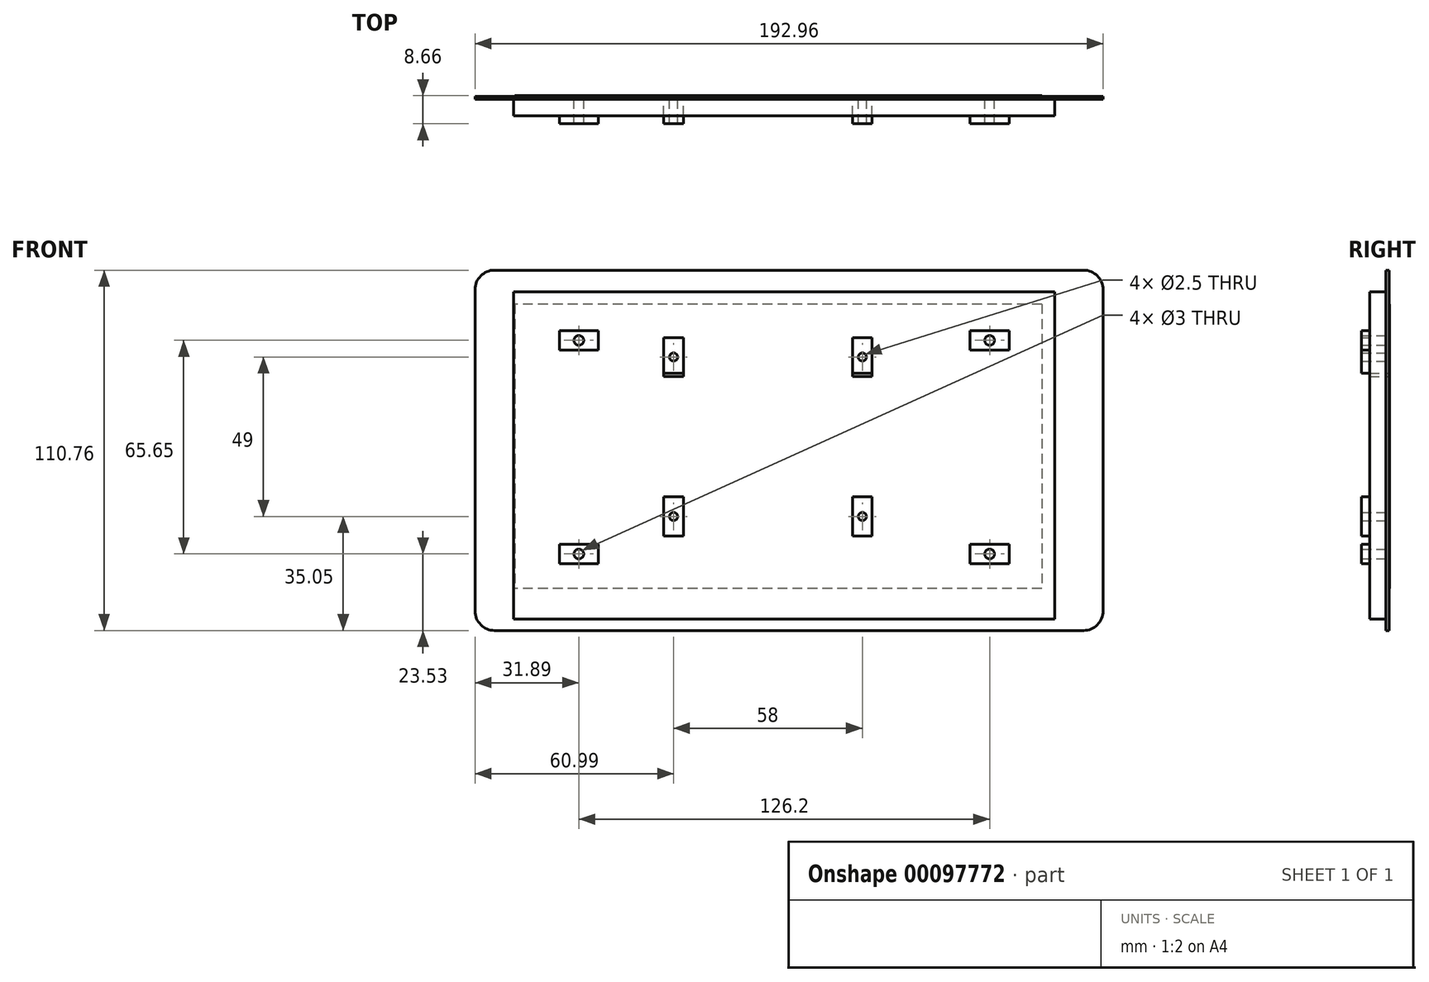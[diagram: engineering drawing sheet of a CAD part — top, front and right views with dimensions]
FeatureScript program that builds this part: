
annotation { "Feature Type Name" : "Feature", "Feature Type Description" : "" }
export const myFeature = defineFeature(function(context is Context, id is Id, definition is map)
    precondition{}
    {
        {
            var Q0;
            Q0=qCreatedBy(makeId("Front.planeOp"),FACE);
            var sketch = newSketch(context, id + "F0", { "sketchPlane" : qUnion([Q0])});
            skLineSegment(sketch, "E0.bottom", {"start": v(90.48, 55.38) * mm, "end": v(-90.48, 55.38) * mm});
            skLineSegment(sketch, "E0.top", {"start": v(90.48, -55.38) * mm, "end": v(-90.48, -55.38) * mm});
            skLineSegment(sketch, "E0.left", {"start": v(96.48, 49.38) * mm, "end": v(96.48, -49.38) * mm});
            skLineSegment(sketch, "E0.right", {"start": v(-96.48, 49.38) * mm, "end": v(-96.48, -49.38) * mm});
            skPoint(sketch, "E0.middle", {"position": v(0, 0) * mm});
            skPoint(sketch, "E1.visualSharp", {"position": v(-96.48, 55.38) * mm});
            skArc(sketch, "E1.filletArc", {"start": v(-90.48, 55.38) * mm, "mid": v(-94.72, 53.62) * mm, "end": v(-96.48, 49.38) * mm});
            skPoint(sketch, "E2.visualSharp", {"position": v(96.48, 55.38) * mm});
            skArc(sketch, "E2.filletArc", {"start": v(96.48, 49.38) * mm, "mid": v(94.72, 53.62) * mm, "end": v(90.48, 55.38) * mm});
            skPoint(sketch, "E3.visualSharp", {"position": v(96.48, -55.38) * mm});
            skArc(sketch, "E3.filletArc", {"start": v(90.48, -55.38) * mm, "mid": v(94.72, -53.62) * mm, "end": v(96.48, -49.38) * mm});
            skPoint(sketch, "E4.visualSharp", {"position": v(-96.48, -55.38) * mm});
            skArc(sketch, "E4.filletArc", {"start": v(-96.48, -49.38) * mm, "mid": v(-94.72, -53.62) * mm, "end": v(-90.48, -55.38) * mm});
            skLineSegment(sketch, "E5", {"start": v(-96.48, 39.83) * mm, "end": v(-84.6, 39.83) * mm});
            skLineSegment(sketch, "E6", {"start": v(-83.46, 55.38) * mm, "end": v(-83.46, 48.75) * mm});
            skLineSegment(sketch, "E7.bottom", {"start": v(-84.6, 48.75) * mm, "end": v(81.6, 48.75) * mm});
            skLineSegment(sketch, "E7.top", {"start": v(-84.6, -51.85) * mm, "end": v(81.6, -51.85) * mm});
            skLineSegment(sketch, "E7.left", {"start": v(-84.6, 48.75) * mm, "end": v(-84.6, -51.85) * mm});
            skLineSegment(sketch, "E7.right", {"start": v(81.6, 48.75) * mm, "end": v(81.6, -51.85) * mm});
            skLineSegment(sketch, "E8", {"start": v(-84.6, 23.64) * mm, "end": v(-64.6, 23.64) * mm});
            skLineSegment(sketch, "E9", {"start": v(-64.6, 23.64) * mm, "end": v(61.6, 23.64) * mm});
            skLineSegment(sketch, "E10", {"start": v(61.6, 23.64) * mm, "end": v(9.4, 23.64) * mm});
            skLineSegment(sketch, "E11", {"start": v(76.4, 55.38) * mm, "end": v(76.4, 33.8) * mm});
            skLineSegment(sketch, "E12", {"start": v(76.4, 33.8) * mm, "end": v(76.4, -31.85) * mm});
            skLineSegment(sketch, "E13", {"start": v(-84.6, 7.67) * mm, "end": v(-83.94, 7.67) * mm});
            skCircle(sketch, "E14", {"center": v(61.6, 33.8) * mm, "radius": 1.5 * mm});
            skCircle(sketch, "E15", {"center": v(-64.6, 33.8) * mm, "radius": 1.5 * mm});
            skCircle(sketch, "E16", {"center": v(61.6, -31.85) * mm, "radius": 1.5 * mm});
            skCircle(sketch, "E17", {"center": v(-64.6, -31.85) * mm, "radius": 1.5 * mm});
            skLineSegment(sketch, "E18", {"start": v(55.09, 48.75) * mm, "end": v(55.09, 28.67) * mm});
            skLineSegment(sketch, "E19", {"start": v(55.09, 28.67) * mm, "end": v(55.09, -20.33) * mm});
            skLineSegment(sketch, "E20", {"start": v(-83.94, 7.67) * mm, "end": v(-35.5, 7.67) * mm});
            skLineSegment(sketch, "E21", {"start": v(-35.5, 7.67) * mm, "end": v(22.5, 7.67) * mm});
            skCircle(sketch, "E22", {"center": v(22.5, 28.67) * mm, "radius": 1.25 * mm});
            skCircle(sketch, "E23", {"center": v(-35.5, 28.67) * mm, "radius": 1.25 * mm});
            skCircle(sketch, "E24", {"center": v(-35.5, -20.33) * mm, "radius": 1.25 * mm});
            skCircle(sketch, "E25", {"center": v(22.5, -20.33) * mm, "radius": 1.25 * mm});
            skLineSegment(sketch, "E26.bottom", {"start": v(-58.6, 36.8) * mm, "end": v(-70.6, 36.8) * mm});
            skLineSegment(sketch, "E26.top", {"start": v(-58.6, 30.8) * mm, "end": v(-70.6, 30.8) * mm});
            skLineSegment(sketch, "E26.left", {"start": v(-58.6, 36.8) * mm, "end": v(-58.6, 30.8) * mm});
            skLineSegment(sketch, "E26.right", {"start": v(-70.6, 36.8) * mm, "end": v(-70.6, 30.8) * mm});
            skLineSegment(sketch, "E27.bottom", {"start": v(67.61, 30.8) * mm, "end": v(55.61, 30.8) * mm});
            skLineSegment(sketch, "E27.top", {"start": v(67.61, 36.8) * mm, "end": v(55.61, 36.8) * mm});
            skLineSegment(sketch, "E27.left", {"start": v(67.61, 30.8) * mm, "end": v(67.61, 36.8) * mm});
            skLineSegment(sketch, "E27.right", {"start": v(55.61, 30.8) * mm, "end": v(55.61, 36.8) * mm});
            skLineSegment(sketch, "E28.bottom", {"start": v(-58.6, -28.85) * mm, "end": v(-70.6, -28.85) * mm});
            skLineSegment(sketch, "E28.top", {"start": v(-58.6, -34.85) * mm, "end": v(-70.6, -34.85) * mm});
            skLineSegment(sketch, "E28.left", {"start": v(-58.6, -28.85) * mm, "end": v(-58.6, -34.85) * mm});
            skLineSegment(sketch, "E28.right", {"start": v(-70.6, -28.85) * mm, "end": v(-70.6, -34.85) * mm});
            skLineSegment(sketch, "E29.bottom", {"start": v(55.61, -28.85) * mm, "end": v(67.61, -28.85) * mm});
            skLineSegment(sketch, "E29.top", {"start": v(55.61, -34.85) * mm, "end": v(67.61, -34.85) * mm});
            skLineSegment(sketch, "E29.left", {"start": v(55.61, -28.85) * mm, "end": v(55.61, -34.85) * mm});
            skLineSegment(sketch, "E29.right", {"start": v(67.61, -28.85) * mm, "end": v(67.61, -34.85) * mm});
            skLineSegment(sketch, "E30.bottom", {"start": v(-32.49, 22.67) * mm, "end": v(-38.49, 22.67) * mm});
            skLineSegment(sketch, "E30.top", {"start": v(-32.49, 34.67) * mm, "end": v(-38.49, 34.67) * mm});
            skLineSegment(sketch, "E30.left", {"start": v(-32.49, 22.67) * mm, "end": v(-32.49, 34.67) * mm});
            skLineSegment(sketch, "E30.right", {"start": v(-38.49, 22.67) * mm, "end": v(-38.49, 34.67) * mm});
            skLineSegment(sketch, "E31.bottom", {"start": v(-32.49, -14.33) * mm, "end": v(-38.49, -14.33) * mm});
            skLineSegment(sketch, "E31.top", {"start": v(-32.49, -26.33) * mm, "end": v(-38.49, -26.33) * mm});
            skLineSegment(sketch, "E31.left", {"start": v(-32.49, -14.33) * mm, "end": v(-32.49, -26.33) * mm});
            skLineSegment(sketch, "E31.right", {"start": v(-38.49, -14.33) * mm, "end": v(-38.49, -26.33) * mm});
            skLineSegment(sketch, "E32.bottom", {"start": v(19.51, 34.67) * mm, "end": v(25.51, 34.67) * mm});
            skLineSegment(sketch, "E32.top", {"start": v(19.51, 22.67) * mm, "end": v(25.51, 22.67) * mm});
            skLineSegment(sketch, "E32.left", {"start": v(19.51, 34.67) * mm, "end": v(19.51, 22.67) * mm});
            skLineSegment(sketch, "E32.right", {"start": v(25.51, 34.67) * mm, "end": v(25.51, 22.67) * mm});
            skLineSegment(sketch, "E33.bottom", {"start": v(19.51, -14.33) * mm, "end": v(25.51, -14.33) * mm});
            skLineSegment(sketch, "E33.top", {"start": v(19.51, -26.33) * mm, "end": v(25.51, -26.33) * mm});
            skLineSegment(sketch, "E33.left", {"start": v(19.51, -14.33) * mm, "end": v(19.51, -26.33) * mm});
            skLineSegment(sketch, "E33.right", {"start": v(25.51, -14.33) * mm, "end": v(25.51, -26.33) * mm});
            skSolve(sketch);
        }
        {
            var Q0;
            {var subQ16=sQuery(id+"F0.wireOp",EDGE,"E7.top");Q0=makeQuery(id+"F0.imprint","IMPRINT",FACE,{"disambiguationData":[TD([[makeQuery(id+"F0.imprint","IMPRINT",EDGE,{"derivedFrom":subQ16}),1.0]])]});}
            var Q1;
            {var subQ17=sQuery(id+"F0.wireOp",EDGE,"E8");Q1=makeQuery(id+"F0.imprint","IMPRINT",FACE,{"disambiguationData":[TD([[makeQuery(id+"F0.imprint","IMPRINT",EDGE,{"derivedFrom":subQ17}),1.0]])]});}
            extrude(context, id + "F1", {"entities" : qUnion([Q0, Q1]), "depth" : 5.96 * mm});
        }
        {
            var Q0;
            Q0=makeQuery(id+"F0.imprint","IMPRINT",FACE,{"disambiguationData":[TD([[makeQuery(id+"F0.imprint","IMPRINT",EDGE,{"derivedFrom":sQuery(id+"F0.wireOp",EDGE,"E15")}),-1.0]])]});
            var Q1;
            Q1=makeQuery(id+"F0.imprint","IMPRINT",FACE,{"disambiguationData":[TD([[makeQuery(id+"F0.imprint","IMPRINT",EDGE,{"derivedFrom":sQuery(id+"F0.wireOp",EDGE,"E23")}),-1.0]])]});
            var Q2;
            Q2=makeQuery(id+"F0.imprint","IMPRINT",FACE,{"disambiguationData":[TD([[makeQuery(id+"F0.imprint","IMPRINT",EDGE,{"derivedFrom":sQuery(id+"F0.wireOp",EDGE,"E22")}),-1.0]])]});
            var Q3;
            Q3=makeQuery(id+"F0.imprint","IMPRINT",FACE,{"disambiguationData":[TD([[makeQuery(id+"F0.imprint","IMPRINT",EDGE,{"derivedFrom":sQuery(id+"F0.wireOp",EDGE,"E14")}),-1.0]])]});
            var Q4;
            Q4=makeQuery(id+"F0.imprint","IMPRINT",FACE,{"disambiguationData":[TD([[makeQuery(id+"F0.imprint","IMPRINT",EDGE,{"derivedFrom":sQuery(id+"F0.wireOp",EDGE,"E25")}),-1.0]])]});
            var Q5;
            Q5=makeQuery(id+"F0.imprint","IMPRINT",FACE,{"disambiguationData":[TD([[makeQuery(id+"F0.imprint","IMPRINT",EDGE,{"derivedFrom":sQuery(id+"F0.wireOp",EDGE,"E16")}),-1.0]])]});
            var Q6;
            Q6=makeQuery(id+"F0.imprint","IMPRINT",FACE,{"disambiguationData":[TD([[makeQuery(id+"F0.imprint","IMPRINT",EDGE,{"derivedFrom":sQuery(id+"F0.wireOp",EDGE,"E24")}),-1.0]])]});
            var Q7;
            Q7=makeQuery(id+"F0.imprint","IMPRINT",FACE,{"disambiguationData":[TD([[makeQuery(id+"F0.imprint","IMPRINT",EDGE,{"derivedFrom":sQuery(id+"F0.wireOp",EDGE,"E17")}),-1.0]])]});
            extrude(context, id + "F2", {"entities" : qUnion([Q0, Q1, Q2, Q3, Q4, Q5, Q6, Q7]), "operationType" : NewBodyOperationType.ADD, "depth" : 8.46 * mm});
        }
        {
            var Q0;
            Q0=makeQuery(id+"F0.imprint","IMPRINT",FACE,{"disambiguationData":[TD([[makeQuery(id+"F0.imprint","IMPRINT",EDGE,{"derivedFrom":sQuery(id+"F0.wireOp",EDGE,"E0.top")}),-1.0]])]});
            var Q1;
            {var subQ1=sQuery(id+"F0.wireOp",EDGE,"E1.filletArc");Q1=makeQuery(id+"F0.imprint","IMPRINT",FACE,{"disambiguationData":[TD([[makeQuery(id+"F0.imprint","IMPRINT",EDGE,{"derivedFrom":subQ1}),1.0]])]});}
            var Q2;
            {var subQ4=sQuery(id+"F0.wireOp",EDGE,"E6");Q2=makeQuery(id+"F0.imprint","IMPRINT",FACE,{"disambiguationData":[TD([[makeQuery(id+"F0.imprint","IMPRINT",EDGE,{"derivedFrom":subQ4}),1.0]])]});}
            extrude(context, id + "F3", {"entities" : qUnion([Q0, Q1, Q2]), "operationType" : NewBodyOperationType.ADD, "depth" : 1 * mm});
        }
        {
            var Q0;
            {var subQ0=sQuery(id+"F0.wireOp",EDGE,"E7.right");var subQ1=sQuery(id+"F0.wireOp",EDGE,"E7.left");var subQ2=sQuery(id+"F0.wireOp",EDGE,"E7.top");var subQ3=sQuery(id+"F0.wireOp",EDGE,"E7.bottom");var subQ4=sQuery(id+"F0.wireOp",EDGE,"E33.right");var subQ5=sQuery(id+"F0.wireOp",EDGE,"E33.left");var subQ6=sQuery(id+"F0.wireOp",EDGE,"E33.top");var subQ7=sQuery(id+"F0.wireOp",EDGE,"E33.bottom");var subQ8=sQuery(id+"F0.wireOp",EDGE,"E31.right");var subQ9=sQuery(id+"F0.wireOp",EDGE,"E31.left");var subQ10=sQuery(id+"F0.wireOp",EDGE,"E31.top");var subQ11=sQuery(id+"F0.wireOp",EDGE,"E31.bottom");var subQ12=sQuery(id+"F0.wireOp",EDGE,"E28.right");var subQ13=sQuery(id+"F0.wireOp",EDGE,"E28.left");var subQ14=sQuery(id+"F0.wireOp",EDGE,"E28.top");var subQ15=sQuery(id+"F0.wireOp",EDGE,"E28.bottom");var subQ16=sQuery(id+"F0.wireOp",EDGE,"E29.right");var subQ17=sQuery(id+"F0.wireOp",EDGE,"E29.left");var subQ18=sQuery(id+"F0.wireOp",EDGE,"E29.top");var subQ19=sQuery(id+"F0.wireOp",EDGE,"E29.bottom");var subQ20=sQuery(id+"F0.wireOp",EDGE,"E26.right");var subQ21=sQuery(id+"F0.wireOp",EDGE,"E26.left");var subQ22=sQuery(id+"F0.wireOp",EDGE,"E26.top");var subQ23=sQuery(id+"F0.wireOp",EDGE,"E26.bottom");var subQ24=sQuery(id+"F0.wireOp",EDGE,"E27.right");var subQ25=sQuery(id+"F0.wireOp",EDGE,"E27.left");var subQ26=sQuery(id+"F0.wireOp",EDGE,"E27.top");var subQ27=sQuery(id+"F0.wireOp",EDGE,"E27.bottom");var subQ28=sQuery(id+"F0.wireOp",EDGE,"E32.right");var subQ29=sQuery(id+"F0.wireOp",EDGE,"E32.left");var subQ30=sQuery(id+"F0.wireOp",EDGE,"E32.bottom");var subQ31=sQuery(id+"F0.wireOp",EDGE,"E30.right");var subQ32=sQuery(id+"F0.wireOp",EDGE,"E30.left");var subQ33=sQuery(id+"F0.wireOp",EDGE,"E30.top");Q0=makeQuery(id+"F3.boolean.opBoolean","MERGE",FACE,{"derivedFrom":[makeQuery(id+"F2.boolean.opBoolean","MERGE",FACE,{"derivedFrom":[makeQuery(id+"F1.opExtrude","CAP_FACE",FACE,{"disambiguationData":[OSD([subQ3,subQ2,subQ1,subQ0,subQ23,subQ22,subQ21,subQ20,subQ27,subQ26,subQ25,subQ24,subQ15,subQ14,subQ13,subQ12,subQ19,subQ18,subQ17,subQ16,sQuery(id+"F0.wireOp",EDGE,"E30.bottom"),subQ33,subQ32,subQ31,subQ11,subQ10,subQ9,subQ8,subQ30,sQuery(id+"F0.wireOp",EDGE,"E32.top"),subQ29,subQ28,subQ7,subQ6,subQ5,subQ4])],"isStart":true}),makeQuery(id+"F2.opExtrude","CAP_FACE",FACE,{"disambiguationData":[OSD([sQuery(id+"F0.wireOp",EDGE,"E9"),sQuery(id+"F0.wireOp",EDGE,"E23"),subQ33,subQ32,subQ31])],"isStart":true}),makeQuery(id+"F2.opExtrude","CAP_FACE",FACE,{"disambiguationData":[OSD([sQuery(id+"F0.wireOp",EDGE,"E10"),sQuery(id+"F0.wireOp",EDGE,"E22"),subQ30,subQ29,subQ28])],"isStart":true}),makeQuery(id+"F2.opExtrude","CAP_FACE",FACE,{"disambiguationData":[OSD([sQuery(id+"F0.wireOp",EDGE,"E14"),subQ27,subQ26,subQ25,subQ24])],"isStart":true}),makeQuery(id+"F2.opExtrude","CAP_FACE",FACE,{"disambiguationData":[OSD([sQuery(id+"F0.wireOp",EDGE,"E15"),subQ23,subQ22,subQ21,subQ20])],"isStart":true}),makeQuery(id+"F2.opExtrude","CAP_FACE",FACE,{"disambiguationData":[OSD([sQuery(id+"F0.wireOp",EDGE,"E16"),subQ19,subQ18,subQ17,subQ16])],"isStart":true}),makeQuery(id+"F2.opExtrude","CAP_FACE",FACE,{"disambiguationData":[OSD([sQuery(id+"F0.wireOp",EDGE,"E17"),subQ15,subQ14,subQ13,subQ12])],"isStart":true}),makeQuery(id+"F2.opExtrude","CAP_FACE",FACE,{"disambiguationData":[OSD([sQuery(id+"F0.wireOp",EDGE,"E24"),subQ11,subQ10,subQ9,subQ8])],"isStart":true}),makeQuery(id+"F2.opExtrude","CAP_FACE",FACE,{"disambiguationData":[OSD([sQuery(id+"F0.wireOp",EDGE,"E25"),subQ7,subQ6,subQ5,subQ4])],"isStart":true})]}),makeQuery(id+"F3.opExtrude","CAP_FACE",FACE,{"disambiguationData":[OSD([sQuery(id+"F0.wireOp",EDGE,"E0.bottom"),sQuery(id+"F0.wireOp",EDGE,"E0.top"),sQuery(id+"F0.wireOp",EDGE,"E0.left"),sQuery(id+"F0.wireOp",EDGE,"E0.right"),sQuery(id+"F0.wireOp",EDGE,"E1.filletArc"),sQuery(id+"F0.wireOp",EDGE,"E2.filletArc"),sQuery(id+"F0.wireOp",EDGE,"E3.filletArc"),sQuery(id+"F0.wireOp",EDGE,"E4.filletArc"),subQ3,subQ2,subQ1,subQ0])],"isStart":true})]});}
            var sketch = newSketch(context, id + "F4", { "sketchPlane" : qUnion([Q0])});
            skLineSegment(sketch, "E34", {"start": v(96.48, 44.4) * mm, "end": v(77.44, 44.4) * mm});
            skLineSegment(sketch, "E35", {"start": v(77.44, 44.4) * mm, "end": v(-77.44, 44.4) * mm});
            skLineSegment(sketch, "E36", {"start": v(84.22, 55.38) * mm, "end": v(84.22, 44.37) * mm});
            skLineSegment(sketch, "E37", {"start": v(84.22, 44.37) * mm, "end": v(84.22, -42.35) * mm});
            skLineSegment(sketch, "E38.bottom", {"start": v(-77.44, 44.4) * mm, "end": v(84.22, 44.4) * mm});
            skLineSegment(sketch, "E38.top", {"start": v(-77.44, -42.35) * mm, "end": v(84.22, -42.35) * mm});
            skLineSegment(sketch, "E38.left", {"start": v(-77.44, 44.4) * mm, "end": v(-77.44, -42.35) * mm});
            skLineSegment(sketch, "E38.right", {"start": v(84.22, 44.4) * mm, "end": v(84.22, -42.35) * mm});
            skSolve(sketch);
        }
        {
            var Q0;
            {var subQ7=sQuery(id+"F4.wireOp",EDGE,"E34");Q0=makeQuery(id+"F4.imprint","IMPRINT",FACE,{"disambiguationData":[TD([[makeQuery(id+"F4.imprint","IMPRINT",EDGE,{"derivedFrom":subQ7}),1.0]])]});}
            cPlane(context, id + "F5", {"entities" : qUnion([Q0]), "cplaneType" : CPlaneType.OFFSET, "offset" : 0 * mm, "width" : 150 * mm, "height" : 150 * mm});
        }
        {
            var Q0;
            Q0=qCreatedBy(id+"F5.planeOp",FACE);
            var sketch = newSketch(context, id + "F6", { "sketchPlane" : qUnion([Q0])});
            skLineSegment(sketch, "E39.bottom", {"start": v(-77.65, 44.93) * mm, "end": v(84.23, 44.93) * mm});
            skLineSegment(sketch, "E39.top", {"start": v(-77.65, -42.43) * mm, "end": v(84.23, -42.43) * mm});
            skLineSegment(sketch, "E39.left", {"start": v(-77.65, 44.93) * mm, "end": v(-77.65, -42.43) * mm});
            skLineSegment(sketch, "E39.right", {"start": v(84.23, 44.93) * mm, "end": v(84.23, -42.43) * mm});
            skSolve(sketch);
        }
        {
            var Q0;
            Q0 = qSketchRegion(id + "F6", true);
            extrude(context, id + "F7", {"entities" : qUnion([Q0]), "depth" : .1 * mm});
        }
        {
            var Q0;
            Q0=makeQuery(id+"F7.opExtrude","CAP_FACE",FACE,{"disambiguationData":[OSD([sQuery(id+"F6.wireOp",EDGE,"E39.bottom"),sQuery(id+"F6.wireOp",EDGE,"E39.top"),sQuery(id+"F6.wireOp",EDGE,"E39.left"),sQuery(id+"F6.wireOp",EDGE,"E39.right")])],"isStart":false});
            var sketch = newSketch(context, id + "F8", { "sketchPlane" : qUnion([Q0])});
            skSolve(sketch);
        }
        {
            var Q0;
            Q0=makeQuery(id+"F8.imprint","IMPRINT",FACE,{"disambiguationData":[TD([[makeQuery(id+"F8.imprint","IMPRINT",EDGE,{"derivedFrom":makeQuery(id+"F7.opExtrude","CAP_EDGE",EDGE,{"disambiguationData":[OSD([sQuery(id+"F6.wireOp",EDGE,"E39.bottom")])],"isStart":false})}),-1.0]])]});
            extrude(context, id + "F9", {"entities" : qUnion([Q0]), "operationType" : NewBodyOperationType.ADD, "depth" : .1 * mm});
        }
    });
